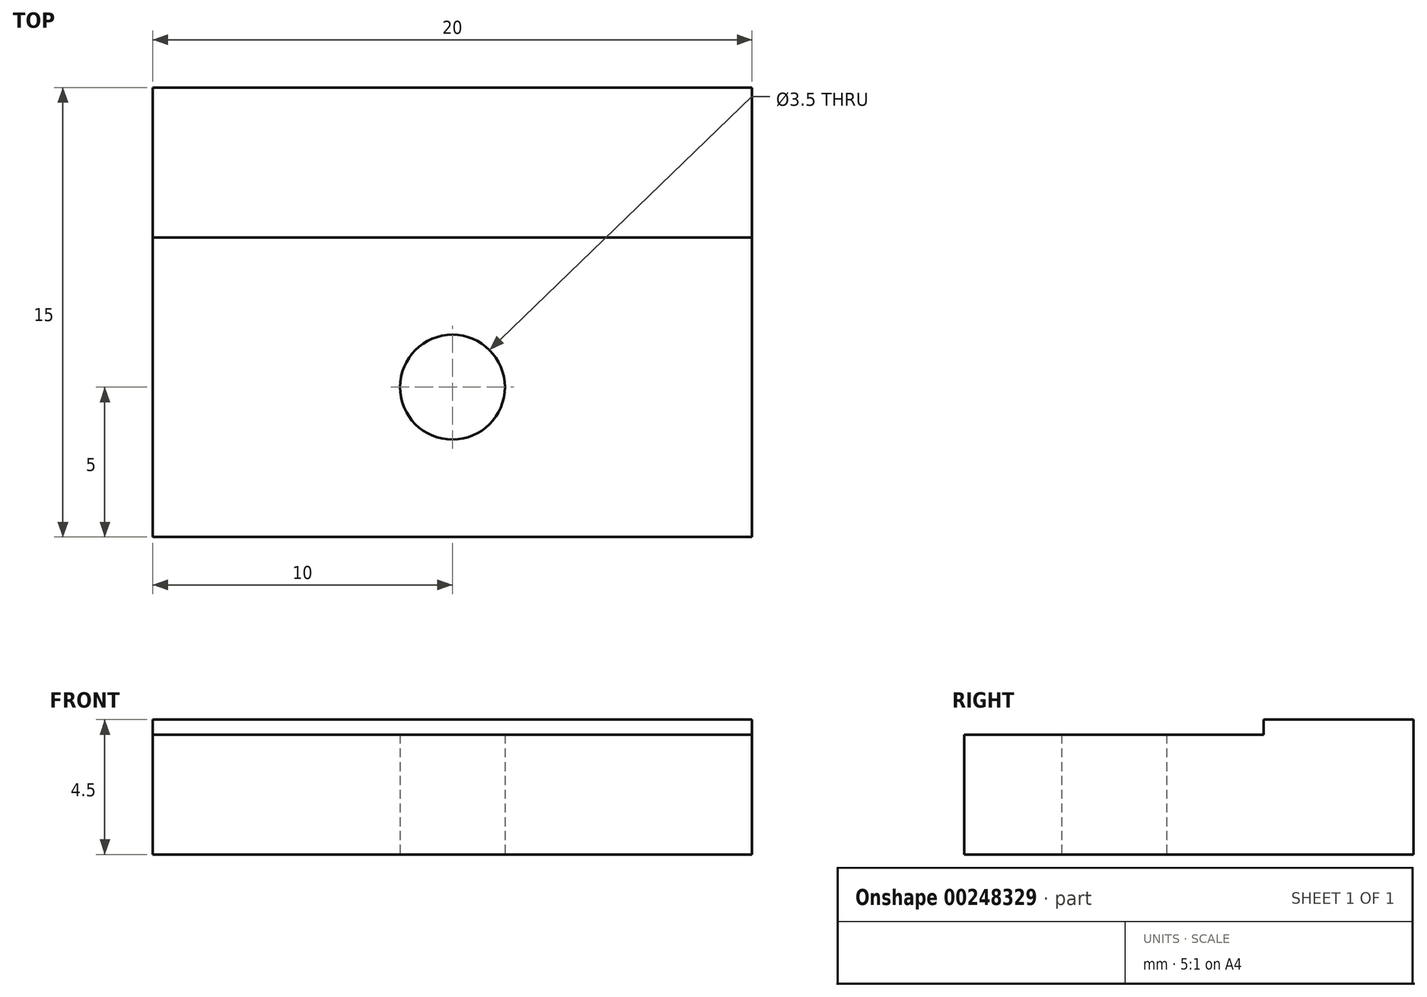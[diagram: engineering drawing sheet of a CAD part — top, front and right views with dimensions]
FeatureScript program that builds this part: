
annotation { "Feature Type Name" : "Feature", "Feature Type Description" : "" }
export const myFeature = defineFeature(function(context is Context, id is Id, definition is map)
    precondition{}
    {
        {
            var Q0;
            Q0=qCreatedBy(makeId("Top.planeOp"),FACE);
            var sketch = newSketch(context, id + "F0", { "sketchPlane" : qUnion([Q0])});
            skLineSegment(sketch, "E0.bottom", {"start": v(0, 0) * mm, "end": v(20, 0) * mm});
            skLineSegment(sketch, "E0.top", {"start": v(0, 15) * mm, "end": v(20, 15) * mm});
            skLineSegment(sketch, "E0.left", {"start": v(0, 0) * mm, "end": v(0, 15) * mm});
            skLineSegment(sketch, "E0.right", {"start": v(20, 0) * mm, "end": v(20, 15) * mm});
            skLineSegment(sketch, "E1", {"start": v(0, 5) * mm, "end": v(20, 5) * mm, "construction": true});
            skLineSegment(sketch, "E2", {"start": v(10, 15) * mm, "end": v(10, 0) * mm, "construction": true});
            skCircle(sketch, "E3", {"center": v(10, 5) * mm, "radius": 1.75 * mm});
            skSolve(sketch);
        }
        {
            var Q0;
            Q0 = qSketchRegion(id + "F0", true);
            extrude(context, id + "F1", {"entities" : qUnion([Q0]), "depth" : 4 * mm, "offsetDistance" : 25 * mm});
        }
        {
            var Q0;
            Q0=makeQuery(id+"F1.opExtrude","CAP_FACE",FACE,{"disambiguationData":[OSD([sQuery(id+"F0.wireOp",EDGE,"E0.bottom"),sQuery(id+"F0.wireOp",EDGE,"E0.top"),sQuery(id+"F0.wireOp",EDGE,"E0.left"),sQuery(id+"F0.wireOp",EDGE,"E0.right"),sQuery(id+"F0.wireOp",EDGE,"E3")])],"isStart":false});
            var sketch = newSketch(context, id + "F2", { "sketchPlane" : qUnion([Q0])});
            skLineSegment(sketch, "E4", {"start": v(0, 10) * mm, "end": v(20, 10) * mm});
            skSolve(sketch);
        }
        {
            var Q0;
            Q0 = qSketchRegion(id + "F2", true);
            var Q1;
            {var subQ0=sQuery(id+"F2.wireOp",EDGE,"E4");Q1=makeQuery(id+"F2.imprint","IMPRINT",FACE,{"disambiguationData":[TD([[makeQuery(id+"F2.imprint","IMPRINT",EDGE,{"derivedFrom":subQ0}),1.0]])]});}
            extrude(context, id + "F3", {"entities" : qUnion([Q0, Q1]), "operationType" : NewBodyOperationType.ADD, "depth" : 0.5 * mm, "offsetDistance" : 25 * mm});
        }
    });
